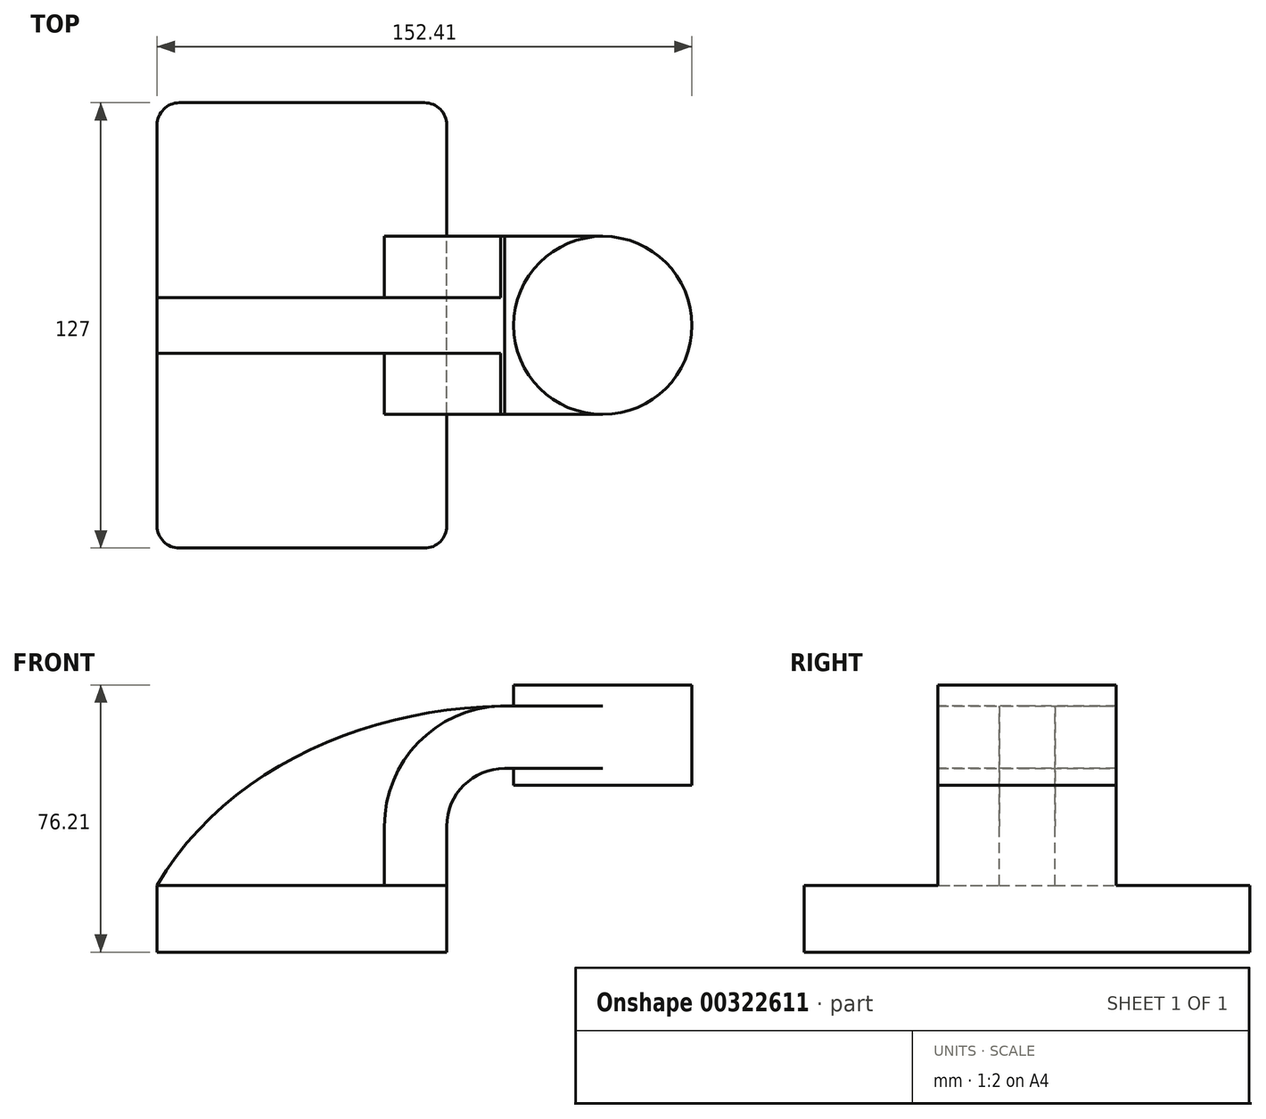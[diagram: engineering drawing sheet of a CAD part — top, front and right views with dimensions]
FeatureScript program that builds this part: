
annotation { "Feature Type Name" : "Feature", "Feature Type Description" : "" }
export const myFeature = defineFeature(function(context is Context, id is Id, definition is map)
    precondition{}
    {
        {
            var Q0;
            Q0=qCreatedBy(makeId("Front.planeOp"),FACE);
            var sketch = newSketch(context, id + "F0", { "sketchPlane" : qUnion([Q0])});
            skLineSegment(sketch, "E0.bottom", {"start": v(-41.28, 9.52) * mm, "end": v(41.28, 9.53) * mm});
            skLineSegment(sketch, "E0.top", {"start": v(-41.28, -9.53) * mm, "end": v(41.28, -9.53) * mm});
            skLineSegment(sketch, "E0.left", {"start": v(-41.28, 9.52) * mm, "end": v(-41.28, -9.53) * mm});
            skLineSegment(sketch, "E0.right", {"start": v(41.28, 9.53) * mm, "end": v(41.28, -9.52) * mm});
            skPoint(sketch, "E0.middle", {"position": v(0, 0) * mm});
            skLineSegment(sketch, "E1.bottom", {"start": v(60.32, 66.68) * mm, "end": v(111.12, 66.68) * mm});
            skLineSegment(sketch, "E1.top", {"start": v(60.32, 38.1) * mm, "end": v(111.12, 38.1) * mm});
            skLineSegment(sketch, "E1.left", {"start": v(60.32, 66.68) * mm, "end": v(60.32, 38.1) * mm});
            skLineSegment(sketch, "E1.right", {"start": v(111.12, 66.68) * mm, "end": v(111.12, 38.1) * mm});
            skPoint(sketch, "E1.middle", {"position": v(85.72, 52.39) * mm});
            skLineSegment(sketch, "E2", {"start": v(41.27, 9.53) * mm, "end": v(41.27, 26.37) * mm});
            skArc(sketch, "E3", {"start": v(41.27, 26.37) * mm, "mid": v(46.11, 38.04) * mm, "end": v(57.78, 42.88) * mm});
            skLineSegment(sketch, "E4", {"start": v(57.78, 42.88) * mm, "end": v(85.72, 42.88) * mm});
            skPoint(sketch, "E4.endSnap0", {"position": v(85.72, 38.1) * mm});
            skArc(sketch, "E5.0", {"start": v(23.5, 26.37) * mm, "mid": v(33.54, 50.61) * mm, "end": v(57.78, 60.66) * mm});
            skLineSegment(sketch, "E5.1", {"start": v(23.5, 9.53) * mm, "end": v(23.5, 26.37) * mm});
            skLineSegment(sketch, "E6.0", {"start": v(57.78, 60.66) * mm, "end": v(85.72, 60.66) * mm});
            skLineSegment(sketch, "E7", {"start": v(85.72, 38.1) * mm, "end": v(85.72, 66.68) * mm});
            skFitSpline(sketch, "E8", {"points": [v(-41.28, 9.52) * mm, v(57.78, 60.66) * mm], "startDerivative": vector(58.25, 99.65) * mm, "endDerivative": vector(119.51, 1.5) * mm});
            skSolve(sketch);
        }
        {
            var Q0;
            Q0=makeQuery(id+"F0.imprint","IMPRINT",FACE,{"disambiguationData":[TD([[makeQuery(id+"F0.imprint","IMPRINT",EDGE,{"derivedFrom":sQuery(id+"F0.wireOp",EDGE,"E0.top")}),1.0]])]});
            extrude(context, id + "F1", {"entities" : qUnion([Q0]), "endBound" : BoundingType.SYMMETRIC, "depth" : 127 * mm});
        }
        {
            var Q0;
            {var subQ1=sQuery(id+"F0.wireOp",EDGE,"E2");Q0=makeQuery(id+"F0.imprint","IMPRINT",FACE,{"disambiguationData":[TD([[makeQuery(id+"F0.imprint","IMPRINT",EDGE,{"derivedFrom":subQ1}),1.0]])]});}
            var Q1;
            {var subQ0=sQuery(id+"F0.wireOp",EDGE,"E6.0");var subQ1=sQuery(id+"F0.wireOp",EDGE,"E1.left");var subQ2=makeQuery(id+"F0.imprint","INTERSECT",VERTEX,{"derivedFrom":[subQ1,subQ0]});Q1=makeQuery(id+"F0.imprint","IMPRINT",FACE,{"disambiguationData":[TD([[makeQuery(id+"F0.imprint","IMPRINT",EDGE,{"disambiguationData":[TD([[subQ2,-1.0]])],"derivedFrom":subQ1}),1.0]])]});}
            extrude(context, id + "F2", {"entities" : qUnion([Q0, Q1]), "operationType" : NewBodyOperationType.ADD, "endBound" : BoundingType.SYMMETRIC, "depth" : 50.8 * mm});
        }
        {
            var Q0;
            {var subQ3=sQuery(id+"F0.wireOp",EDGE,"E5.1");Q0=makeQuery(id+"F0.imprint","IMPRINT",FACE,{"disambiguationData":[TD([[makeQuery(id+"F0.imprint","IMPRINT",EDGE,{"derivedFrom":subQ3}),1.0]])]});}
            extrude(context, id + "F3", {"entities" : qUnion([Q0]), "operationType" : NewBodyOperationType.ADD, "endBound" : BoundingType.SYMMETRIC, "depth" : 15.88 * mm});
        }
        {
            var Q0;
            {var subQ4=sQuery(id+"F0.wireOp",EDGE,"E1.right");Q0=makeQuery(id+"F0.imprint","IMPRINT",FACE,{"disambiguationData":[TD([[makeQuery(id+"F0.imprint","IMPRINT",EDGE,{"derivedFrom":subQ4}),-1.0]])]});}
            var Q1;
            Q1=sQuery(id+"F0.wireOp",EDGE,"E7");
            revolve(context, id + "F4", {"operationType" : NewBodyOperationType.ADD, "entities" : qUnion([Q0]), "axis" : qUnion([Q1]), "revolveType" : RevolveType.FULL});
        }
        {
            var Q0;
            Q0=makeQuery(id+"F1.opExtrude","CAP_EDGE",EDGE,{"disambiguationData":[OSD([sQuery(id+"F0.wireOp",EDGE,"E0.right")])],"isStart":false});
            var Q1;
            Q1=makeQuery(id+"F1.opExtrude","CAP_EDGE",EDGE,{"disambiguationData":[OSD([sQuery(id+"F0.wireOp",EDGE,"E0.left")])],"isStart":false});
            var Q2;
            Q2=makeQuery(id+"F1.opExtrude","CAP_EDGE",EDGE,{"disambiguationData":[OSD([sQuery(id+"F0.wireOp",EDGE,"E0.right")])],"isStart":true});
            var Q3;
            Q3=makeQuery(id+"F1.opExtrude","CAP_EDGE",EDGE,{"disambiguationData":[OSD([sQuery(id+"F0.wireOp",EDGE,"E0.left")])],"isStart":true});
            fillet(context, id + "F5", {"entities" : qUnion([Q0, Q1, Q2, Q3]), "radius" : 6.35 * mm, "tangentPropagation" : true, "allowEdgeOverflow" : false});
        }
    });
